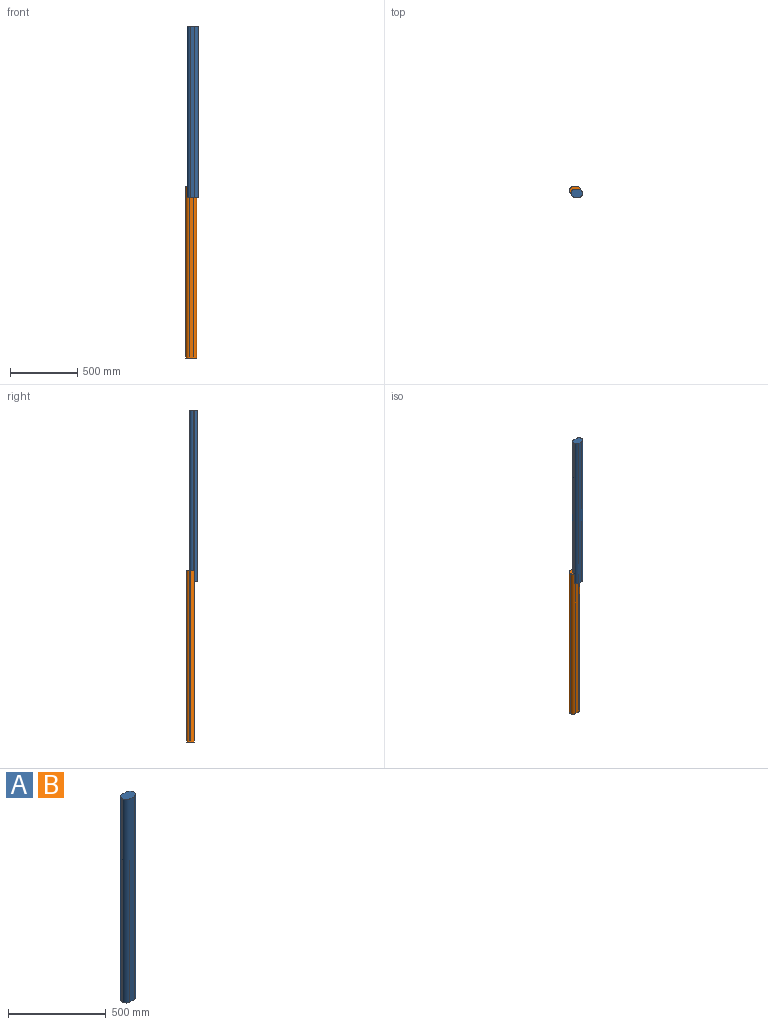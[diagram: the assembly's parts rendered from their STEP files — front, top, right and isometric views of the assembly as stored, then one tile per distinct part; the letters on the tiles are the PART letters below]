
ASSEMBLY  parts=2 mates=1
PART A: 10 faces, bbox 81.4x58.1x1270 mm
  f0: plane 1270x7.31mm, normal (-1,0,0), area 9284.5mm2, adj f4,f5,f6,f9
  f1: plane 1270x30.56mm, normal (0,-1,0), area 38812.5mm2, adj f4,f5,f6,f7
  f2: plane 1270x7.31mm, normal (1,0,0), area 9284.5mm2, adj f4,f5,f7,f8
  f3: plane 1270x30.56mm, normal (0,1,0), area 38812.5mm2, adj f4,f5,f8,f9
  f4: plane 81.36x58.11mm, normal (0,0,1), area 4174.1mm2, adj f0,f1,f2,f3,f6,f7,f8,f9
  f5: plane 81.36x58.11mm, normal (0,0,-1), area 4174.1mm2, adj f0,f1,f2,f3,f6,f7,f8,f9
  f6: cylinder r=25.4mm len=1270mm, axis (0,0,1), area 50670.7mm2, adj f0,f1,f4,f5
  f7: cylinder r=25.4mm len=1270mm, axis (0,0,-1), area 50670.7mm2, adj f1,f2,f4,f5
  f8: cylinder r=25.4mm len=1270mm, axis (0,0,1), area 50670.7mm2, adj f2,f3,f4,f5
  f9: cylinder r=25.4mm len=1270mm, axis (0,0,-1), area 50670.7mm2, adj f0,f3,f4,f5
PART B: same geometry as A
PLACE A rot(axis=(-1,0,0),180deg) t=(-196.01,301.95,2415.15)mm
PLACE B t=(-208.4,266.64,-46.2)mm
MATE parallel A.f4 <-> B.f4  axis (0,0,-1) through (-140.05,243.84,1145.15)mm
